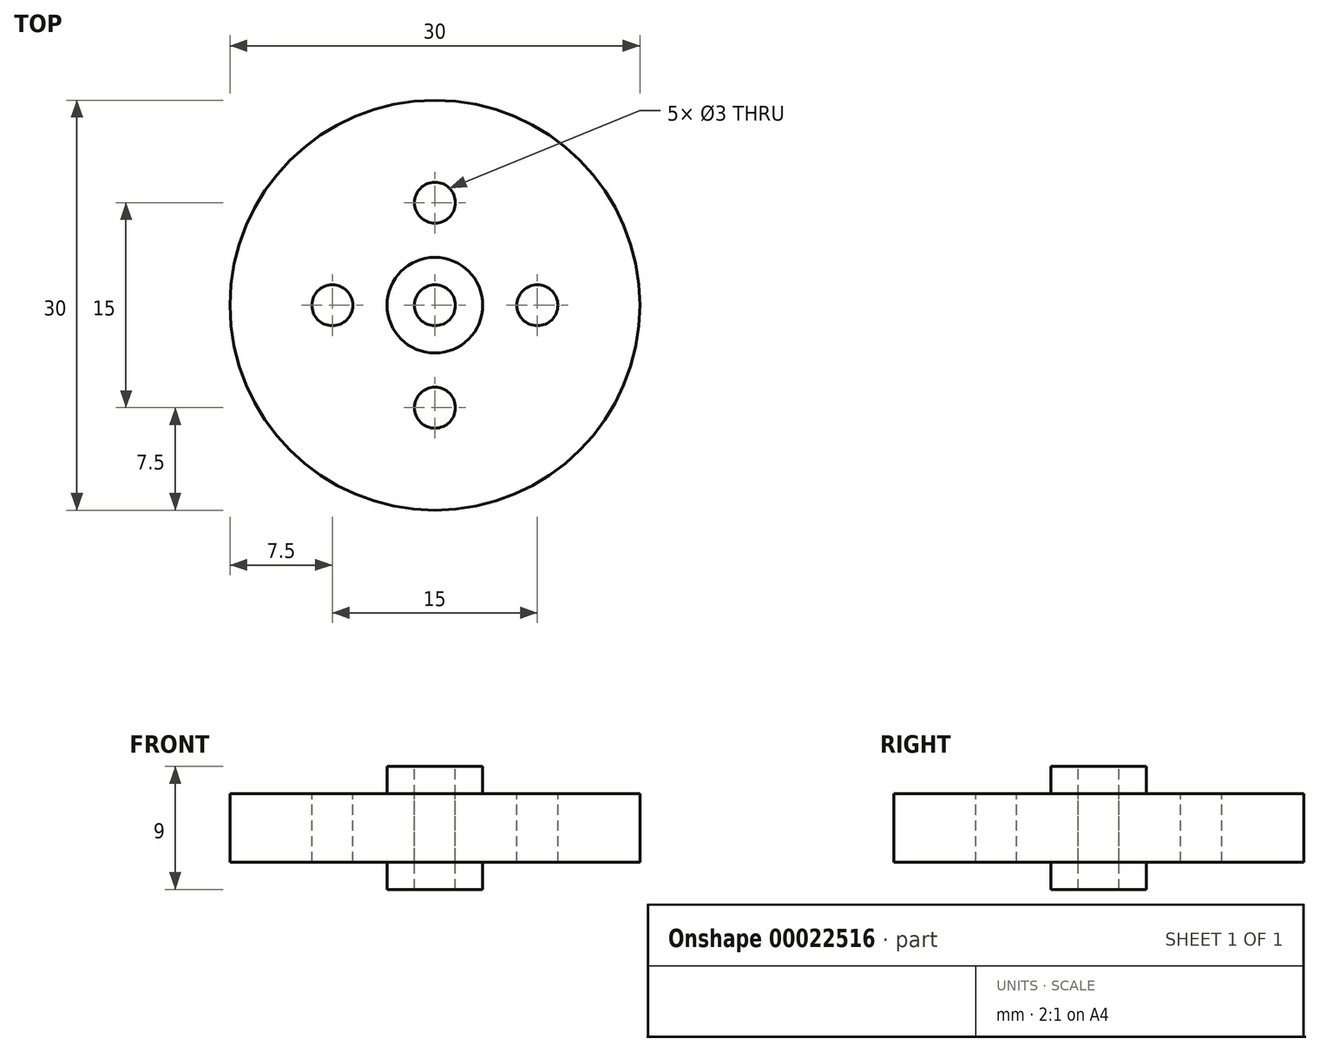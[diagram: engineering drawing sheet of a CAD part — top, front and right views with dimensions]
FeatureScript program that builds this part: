
annotation { "Feature Type Name" : "Feature", "Feature Type Description" : "" }
export const myFeature = defineFeature(function(context is Context, id is Id, definition is map)
    precondition{}
    {
        {
            var Q0;
            Q0=qCreatedBy(makeId("Top.planeOp"),FACE);
            var sketch = newSketch(context, id + "F0", { "sketchPlane" : qUnion([Q0])});
            skCircle(sketch, "E0", {"center": v(0, 0) * mm, "radius": 15 * mm});
            skSolve(sketch);
        }
        {
            var Q0;
            Q0 = qSketchRegion(id + "F0", true);
            extrude(context, id + "F1", {"entities" : qUnion([Q0]), "depth" : 5 * mm});
        }
        {
            var Q0;
            Q0=makeQuery(id+"F1.opExtrude","CAP_FACE",FACE,{"disambiguationData":[OSD([sQuery(id+"F0.wireOp",EDGE,"E0")])],"isStart":false});
            var sketch = newSketch(context, id + "F2", { "sketchPlane" : qUnion([Q0])});
            skLineSegment(sketch, "E1", {"start": v(0, 15) * mm, "end": v(0, 7.5) * mm});
            skCircle(sketch, "E2", {"center": v(0, 7.5) * mm, "radius": 1.5 * mm});
            skCircle(sketch, "E3.1.0", {"center": v(-7.5, 0) * mm, "radius": 1.5 * mm});
            skCircle(sketch, "E3.2.0", {"center": v(0, -7.5) * mm, "radius": 1.5 * mm});
            skCircle(sketch, "E3.3.0", {"center": v(7.5, 0) * mm, "radius": 1.5 * mm});
            skPoint(sketch, "E3.center", {"position": v(0, 0) * mm});
            skCircle(sketch, "E4", {"center": v(0, 0) * mm, "radius": 3.5 * mm});
            skSolve(sketch);
        }
        {
            var Q0;
            Q0=makeQuery(id+"F2.imprint","IMPRINT",FACE,{"disambiguationData":[TD([[makeQuery(id+"F2.imprint","IMPRINT",EDGE,{"derivedFrom":sQuery(id+"F2.wireOp",EDGE,"E4")}),1.0]])]});
            extrude(context, id + "F3", {"entities" : qUnion([Q0]), "operationType" : NewBodyOperationType.ADD, "depth" : 2 * mm});
        }
        {
            var Q0;
            Q0=makeQuery(id+"F2.imprint","IMPRINT",FACE,{"disambiguationData":[TD([[makeQuery(id+"F2.imprint","IMPRINT",EDGE,{"derivedFrom":sQuery(id+"F2.wireOp",EDGE,"E2")}),1.0]])]});
            var Q1;
            Q1=makeQuery(id+"F2.imprint","IMPRINT",FACE,{"disambiguationData":[TD([[makeQuery(id+"F2.imprint","IMPRINT",EDGE,{"derivedFrom":sQuery(id+"F2.wireOp",EDGE,"E3.1.0")}),1.0]])]});
            var Q2;
            Q2=makeQuery(id+"F2.imprint","IMPRINT",FACE,{"disambiguationData":[TD([[makeQuery(id+"F2.imprint","IMPRINT",EDGE,{"derivedFrom":sQuery(id+"F2.wireOp",EDGE,"E3.2.0")}),1.0]])]});
            var Q3;
            Q3=makeQuery(id+"F2.imprint","IMPRINT",FACE,{"disambiguationData":[TD([[makeQuery(id+"F2.imprint","IMPRINT",EDGE,{"derivedFrom":sQuery(id+"F2.wireOp",EDGE,"E3.3.0")}),1.0]])]});
            extrude(context, id + "F4", {"entities" : qUnion([Q0, Q1, Q2, Q3]), "operationType" : NewBodyOperationType.REMOVE, "oppositeDirection" : true, "depth" : 5 * mm});
        }
        {
            var Q0;
            Q0=makeQuery(id+"F3.opExtrude","CAP_FACE",FACE,{"disambiguationData":[OSD([sQuery(id+"F2.wireOp",EDGE,"E4")])],"isStart":false});
            var sketch = newSketch(context, id + "F5", { "sketchPlane" : qUnion([Q0])});
            skCircle(sketch, "E5", {"center": v(0, 0) * mm, "radius": 1.5 * mm});
            skSolve(sketch);
        }
        {
            var Q0;
            Q0=makeQuery(id+"F5.imprint","IMPRINT",FACE,{"disambiguationData":[TD([[makeQuery(id+"F5.imprint","IMPRINT",EDGE,{"derivedFrom":sQuery(id+"F5.wireOp",EDGE,"E5")}),1.0]])]});
            extrude(context, id + "F6", {"entities" : qUnion([Q0]), "operationType" : NewBodyOperationType.REMOVE, "oppositeDirection" : true, "depth" : 10 * mm});
        }
        {
            var Q0;
            Q0=makeQuery(id+"F1.opExtrude","SWEPT_BODY",BODY,{"disambiguationData":[OSD([sQuery(id+"F0.wireOp",EDGE,"E0")])]});
            transform(context, id + "F7", {"entities" : qUnion([Q0]), "transformType" : TransformType.TRANSLATION_3D, "dx" : 0 * mm, "dy" : 0 * mm, "dz" : 0 * mm, "makeCopy" : true});
        }
        {
            var Q0;
            Q0=makeQuery(id+"F1.opExtrude","CAP_FACE",FACE,{"disambiguationData":[OSD([sQuery(id+"F0.wireOp",EDGE,"E0")])],"isStart":true});
            var sketch = newSketch(context, id + "F8", { "sketchPlane" : qUnion([Q0])});
            skCircle(sketch, "E6", {"center": v(0, 0) * mm, "radius": 3.5 * mm});
            skSolve(sketch);
        }
        {
            var Q0;
            Q0=makeQuery(id+"F8.imprint","IMPRINT",FACE,{"disambiguationData":[TD([[makeQuery(id+"F8.imprint","IMPRINT",EDGE,{"derivedFrom":sQuery(id+"F8.wireOp",EDGE,"E6")}),1.0]])]});
            extrude(context, id + "F9", {"entities" : qUnion([Q0]), "operationType" : NewBodyOperationType.ADD, "depth" : 2 * mm});
        }
    });
